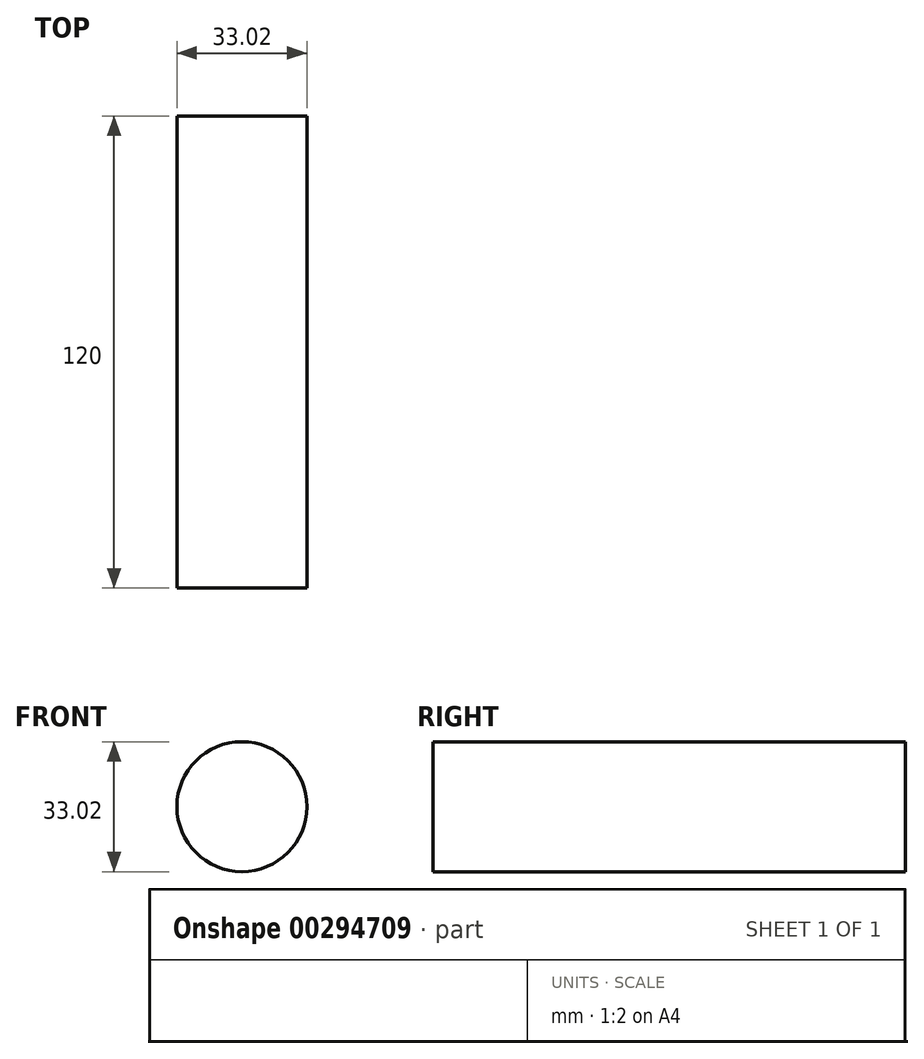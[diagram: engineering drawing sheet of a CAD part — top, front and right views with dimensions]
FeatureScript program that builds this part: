
annotation { "Feature Type Name" : "Feature", "Feature Type Description" : "" }
export const myFeature = defineFeature(function(context is Context, id is Id, definition is map)
    precondition{}
    {
        {
            var Q0;
            Q0=qCreatedBy(makeId("Front.planeOp"),FACE);
            var sketch = newSketch(context, id + "F0", { "sketchPlane" : qUnion([Q0])});
            skCircle(sketch, "E0", {"center": v(0, 0) * mm, "radius": 16.51 * mm});
            skSolve(sketch);
        }
        {
            var Q0;
            Q0 = qSketchRegion(id + "F0", true);
            extrude(context, id + "F1", {"entities" : qUnion([Q0]), "depth" : 120 * mm});
        }
    });
